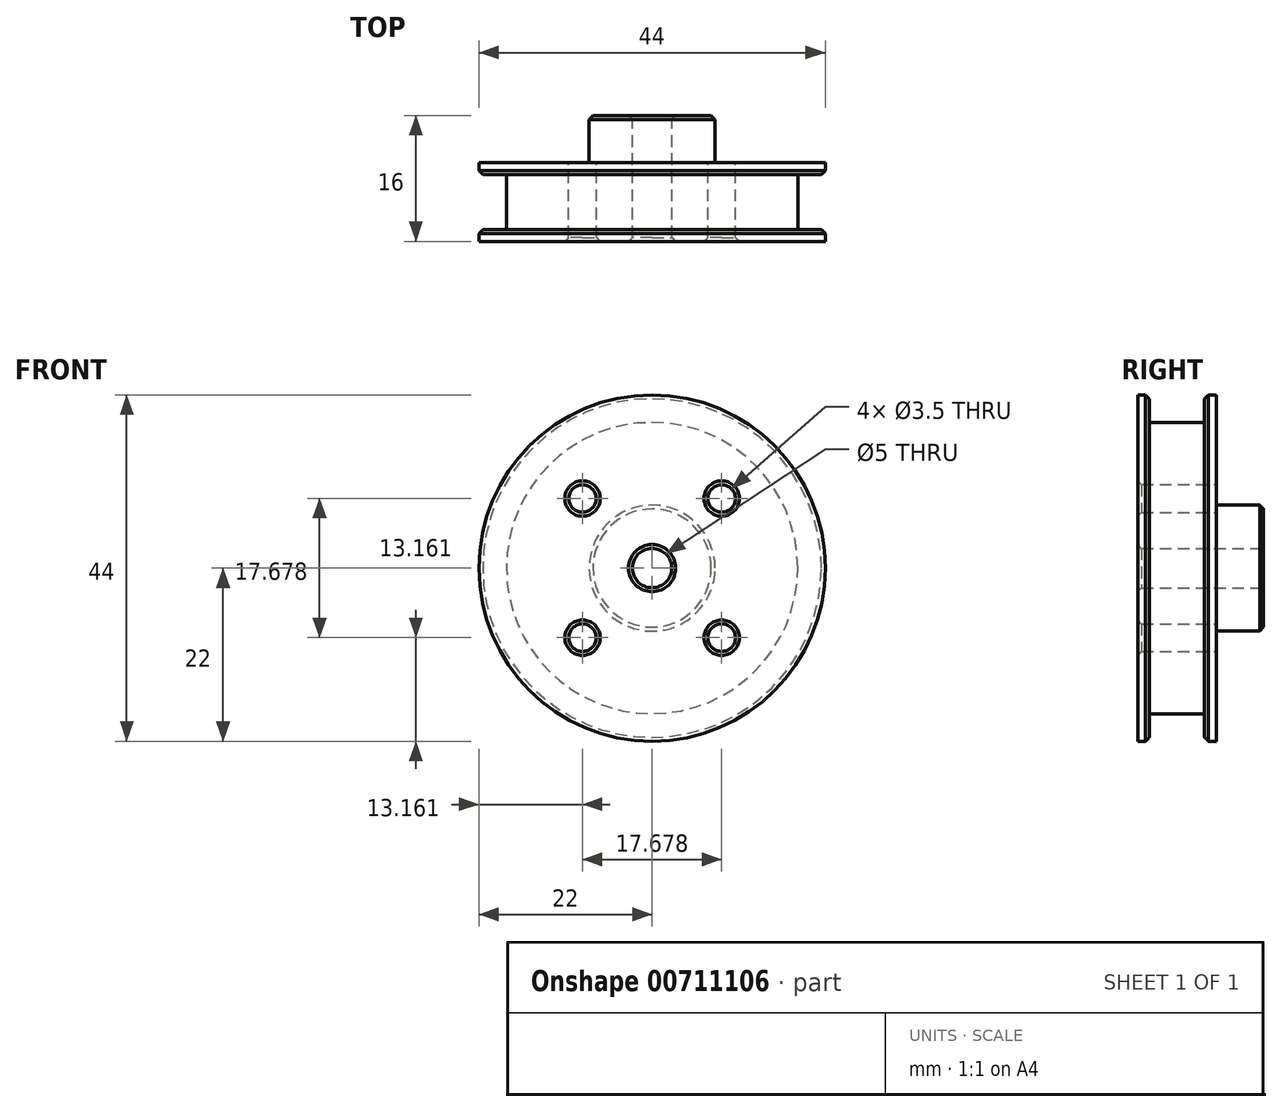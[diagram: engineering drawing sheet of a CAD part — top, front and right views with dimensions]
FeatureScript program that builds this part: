
annotation { "Feature Type Name" : "Feature", "Feature Type Description" : "" }
export const myFeature = defineFeature(function(context is Context, id is Id, definition is map)
    precondition{}
    {
        {
            var Q0;
            Q0=qCreatedBy(makeId("Front.planeOp"),FACE);
            var sketch = newSketch(context, id + "F0", { "sketchPlane" : qUnion([Q0])});
            skCircle(sketch, "E0", {"center": v(0, 0) * mm, "radius": 22 * mm});
            skSolve(sketch);
        }
        {
            var Q0;
            Q0 = qSketchRegion(id + "F0", true);
            extrude(context, id + "F1", {"entities" : qUnion([Q0]), "endBound" : BoundingType.SYMMETRIC, "depth" : 10 * mm, "offsetDistance" : 25 * mm});
        }
        {
            var Q0;
            Q0=qCreatedBy(makeId("Front.planeOp"),FACE);
            var sketch = newSketch(context, id + "F2", { "sketchPlane" : qUnion([Q0])});
            skCircle(sketch, "E1", {"center": v(0, 0) * mm, "radius": 18.5 * mm});
            skCircle(sketch, "E2", {"center": v(0, 0) * mm, "radius": 30.43 * mm});
            skSolve(sketch);
        }
        {
            var Q0;
            Q0 = qSketchRegion(id + "F2", true);
            extrude(context, id + "F3", {"entities" : qUnion([Q0]), "operationType" : NewBodyOperationType.REMOVE, "endBound" : BoundingType.SYMMETRIC, "depth" : 7 * mm, "offsetDistance" : 25 * mm});
        }
        {
            var Q0;
            Q0=makeQuery(id+"F1.opExtrude","CAP_FACE",FACE,{"disambiguationData":[OSD([sQuery(id+"F0.wireOp",EDGE,"E0")])],"isStart":true});
            var sketch = newSketch(context, id + "F4", { "sketchPlane" : qUnion([Q0])});
            skCircle(sketch, "E3", {"center": v(0, 0) * mm, "radius": 8 * mm});
            skSolve(sketch);
        }
        {
            var Q0;
            Q0 = qSketchRegion(id + "F4", true);
            extrude(context, id + "F5", {"entities" : qUnion([Q0]), "operationType" : NewBodyOperationType.ADD, "depth" : 6 * mm, "offsetDistance" : 25 * mm});
        }
        {
            var Q0;
            Q0=makeQuery(id+"F5.opExtrude","CAP_FACE",FACE,{"disambiguationData":[OSD([sQuery(id+"F4.wireOp",EDGE,"E3")])],"isStart":false});
            var sketch = newSketch(context, id + "F6", { "sketchPlane" : qUnion([Q0])});
            skCircle(sketch, "E4", {"center": v(0, 0) * mm, "radius": 2.5 * mm});
            skSolve(sketch);
        }
        {
            var Q0;
            Q0 = qSketchRegion(id + "F6", true);
            extrude(context, id + "F7", {"entities" : qUnion([Q0]), "operationType" : NewBodyOperationType.REMOVE, "endBound" : BoundingType.THROUGH_ALL, "oppositeDirection" : true, "depth" : 25 * mm, "offsetDistance" : 25 * mm});
        }
        {
            var Q0;
            Q0=makeQuery(id+"F5.opExtrude","CAP_FACE",FACE,{"disambiguationData":[OSD([sQuery(id+"F4.wireOp",EDGE,"E3")])],"isStart":false});
            var Q1;
            Q1=makeQuery(id+"F5.opExtrude","CAP_EDGE",EDGE,{"disambiguationData":[OSD([sQuery(id+"F4.wireOp",EDGE,"E3")])],"isStart":true});
            var Q2;
            Q2=makeQuery(id+"F3.boolean.opBoolean","INTERSECT",EDGE,{"derivedFrom":[makeQuery(id+"F1.opExtrude","SWEPT_FACE",FACE,{"disambiguationData":[OSD([sQuery(id+"F0.wireOp",EDGE,"E0")])]}),makeQuery(id+"F3.opExtrude","CAP_FACE",FACE,{"disambiguationData":[OSD([sQuery(id+"F2.wireOp",EDGE,"E1"),sQuery(id+"F2.wireOp",EDGE,"E2")])],"isStart":true})]});
            var Q3;
            Q3=makeQuery(id+"F3.boolean.opBoolean","INTERSECT",EDGE,{"derivedFrom":[makeQuery(id+"F1.opExtrude","SWEPT_FACE",FACE,{"disambiguationData":[OSD([sQuery(id+"F0.wireOp",EDGE,"E0")])]}),makeQuery(id+"F3.opExtrude","CAP_FACE",FACE,{"disambiguationData":[OSD([sQuery(id+"F2.wireOp",EDGE,"E1"),sQuery(id+"F2.wireOp",EDGE,"E2")])],"isStart":false})]});
            var Q4;
            Q4=makeQuery(id+"F7.boolean.opBoolean","INTERSECT",EDGE,{"derivedFrom":[makeQuery(id+"F1.opExtrude","CAP_FACE",FACE,{"disambiguationData":[OSD([sQuery(id+"F0.wireOp",EDGE,"E0")])],"isStart":false}),makeQuery(id+"F7.opExtrude","SWEPT_FACE",FACE,{"disambiguationData":[OSD([sQuery(id+"F6.wireOp",EDGE,"E4")])]})]});
            chamfer(context, id + "F8", {"entities" : qUnion([Q0, Q1, Q2, Q3, Q4]), "width" : 0.5 * mm, "tangentPropagation" : true});
        }
        {
            var Q0;
            Q0=makeQuery(id+"F1.opExtrude","CAP_FACE",FACE,{"disambiguationData":[OSD([sQuery(id+"F0.wireOp",EDGE,"E0")])],"isStart":true});
            var sketch = newSketch(context, id + "F9", { "sketchPlane" : qUnion([Q0])});
            skCircle(sketch, "E5", {"center": v(-8.84, 8.84) * mm, "radius": 1.75 * mm});
            skLineSegment(sketch, "E6", {"start": v(-22, 0) * mm, "end": v(0, 0) * mm, "construction": true});
            skLineSegment(sketch, "E7", {"start": v(0, 0) * mm, "end": v(-8.84, 8.84) * mm, "construction": true});
            skCircle(sketch, "E8.1.0", {"center": v(-8.84, -8.84) * mm, "radius": 1.75 * mm});
            skCircle(sketch, "E8.2.0", {"center": v(8.84, -8.84) * mm, "radius": 1.75 * mm});
            skCircle(sketch, "E8.3.0", {"center": v(8.84, 8.84) * mm, "radius": 1.75 * mm});
            skPoint(sketch, "E8.center", {"position": v(0, 0) * mm});
            skSolve(sketch);
        }
        {
            var Q0;
            Q0 = qSketchRegion(id + "F9", true);
            extrude(context, id + "F10", {"entities" : qUnion([Q0]), "operationType" : NewBodyOperationType.REMOVE, "endBound" : BoundingType.THROUGH_ALL, "oppositeDirection" : true, "depth" : 25 * mm, "offsetDistance" : 25 * mm});
        }
        {
            var Q0;
            Q0=makeQuery(id+"F10.boolean.opBoolean","INTERSECT",EDGE,{"derivedFrom":[makeQuery(id+"F1.opExtrude","CAP_FACE",FACE,{"disambiguationData":[OSD([sQuery(id+"F0.wireOp",EDGE,"E0")])],"isStart":false}),makeQuery(id+"F10.opExtrude","SWEPT_FACE",FACE,{"disambiguationData":[OSD([sQuery(id+"F9.wireOp",EDGE,"E8.3.0")])]})]});
            var Q1;
            Q1=makeQuery(id+"F10.boolean.opBoolean","INTERSECT",EDGE,{"derivedFrom":[makeQuery(id+"F1.opExtrude","CAP_FACE",FACE,{"disambiguationData":[OSD([sQuery(id+"F0.wireOp",EDGE,"E0")])],"isStart":false}),makeQuery(id+"F10.opExtrude","SWEPT_FACE",FACE,{"disambiguationData":[OSD([sQuery(id+"F9.wireOp",EDGE,"E8.2.0")])]})]});
            var Q2;
            Q2=makeQuery(id+"F10.boolean.opBoolean","INTERSECT",EDGE,{"derivedFrom":[makeQuery(id+"F1.opExtrude","CAP_FACE",FACE,{"disambiguationData":[OSD([sQuery(id+"F0.wireOp",EDGE,"E0")])],"isStart":false}),makeQuery(id+"F10.opExtrude","SWEPT_FACE",FACE,{"disambiguationData":[OSD([sQuery(id+"F9.wireOp",EDGE,"E8.1.0")])]})]});
            var Q3;
            Q3=makeQuery(id+"F10.boolean.opBoolean","INTERSECT",EDGE,{"derivedFrom":[makeQuery(id+"F1.opExtrude","CAP_FACE",FACE,{"disambiguationData":[OSD([sQuery(id+"F0.wireOp",EDGE,"E0")])],"isStart":false}),makeQuery(id+"F10.opExtrude","SWEPT_FACE",FACE,{"disambiguationData":[OSD([sQuery(id+"F9.wireOp",EDGE,"E5")])]})]});
            var Q4;
            Q4=makeQuery(id+"F10.boolean.opBoolean","COPY",EDGE,{"derivedFrom":makeQuery(id+"F10.opExtrude","CAP_EDGE",EDGE,{"disambiguationData":[OSD([sQuery(id+"F9.wireOp",EDGE,"E5")])],"isStart":true})});
            var Q5;
            Q5=makeQuery(id+"F10.boolean.opBoolean","COPY",EDGE,{"derivedFrom":makeQuery(id+"F10.opExtrude","CAP_EDGE",EDGE,{"disambiguationData":[OSD([sQuery(id+"F9.wireOp",EDGE,"E8.3.0")])],"isStart":true})});
            var Q6;
            Q6=makeQuery(id+"F10.boolean.opBoolean","COPY",EDGE,{"derivedFrom":makeQuery(id+"F10.opExtrude","CAP_EDGE",EDGE,{"disambiguationData":[OSD([sQuery(id+"F9.wireOp",EDGE,"E8.2.0")])],"isStart":true})});
            var Q7;
            Q7=makeQuery(id+"F10.boolean.opBoolean","COPY",EDGE,{"derivedFrom":makeQuery(id+"F10.opExtrude","CAP_EDGE",EDGE,{"disambiguationData":[OSD([sQuery(id+"F9.wireOp",EDGE,"E8.1.0")])],"isStart":true})});
            chamfer(context, id + "F11", {"entities" : qUnion([Q0, Q1, Q2, Q3, Q4, Q5, Q6, Q7]), "width" : 0.5 * mm, "tangentPropagation" : true});
        }
    });
